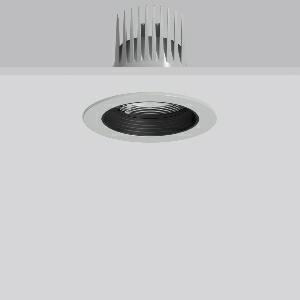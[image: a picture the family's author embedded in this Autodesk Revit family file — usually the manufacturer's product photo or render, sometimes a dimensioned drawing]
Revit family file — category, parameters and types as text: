
# Revit family: heledon_maxi_e_901768_004_cb93
name_source: partatom
category: Lighting Fixtures
units: mm (PartAtom-declared; Revit-internal decimal feet)

## family parameters
Cut with Voids When Loaded = No
Host = Face
Light Source = No
Part Type = Normal
Room Calculation Point = No
Round Connector Dimension = Use Diameter
Shared = No

## types (1)
- HELEDON maxi E (1 x LED Modul 930, 3500 lm, 3000)
    Apparent Load = 35 VA
    Approval mark = CE
    CIE Flux Codes = 96 100 100 100 100
    Color Rendering = 90
    Color Temperature = 3000
    Default Elevation = 1800 mm
    Description = Series: HELEDON maxi
Round recessed downlight. Housing: die-cast aluminium, powder-coated. Black plastic ring and recessed LED to prevent glare from the side. Optical assembly with lens made of plastic (polycarbonate) for the best homogeneous light distribution - can be changed without tools. Best colour rendering index Ra>90. Suitable for Recessed ceiling mounting. Installation without tools thanks to spring fastening system. Including separate LED converter with connecting cable 600 mm.High quality converter without flickering and stroboscopic effect. Through-wiring box (5 pole) available as accessory. The following accessories can be mounted without use of tools: interchangeable lenses, decorative glasses, honeycomb louvre, clear and frosted diffusers, white interchangeable plastic ring. 
Colour: silver
Diameter: 162 mm
Height: 3 mm
Cut-out diameter: 152 mm
Recess height: 200 mm
Luminaire: recess height: 135 mm
Lamp: LED
Socket: without socket
Colour temperature: 3000K
Colour rendering index (CRI): 92
System power: 35 W
Rated luminous flux: 3500 lm
Luminous efficiency: 100 lm/W
Control gear: Regulated power supply
Protection class: II
Type of protection: IP 20
    Height = 0 mm  [stored 0 ft]
    Lamp = 1 x LED Modul 930
    Lamp Light Flux = 3500 lm
    Lamp count = 1
    Length = 162 mm
    Lifetime = 50000 h
    Luminous efficacy = 100 lm/W
    Manufacturer = RZB
    ModVariant = No
    Model = 901768.004
    Mounting Place = Ceiling
    Mounting Type = Recessed
    Number of Poles = 1
    OnlyDefault = Yes
    Power Factor = 1
    Product Name = HELEDON maxi E
    Product group = Recessed downlights
    ProductGroupID = 402
    Protection Class = Protection class II
    Protection Degree = IP 20
    RLX_Detail_Level = 1
    RLX_Emergency_Light_Flux = 0 lm
    RLX_Emergency_Type = 0
    RLX_Emergency_Type_DB = No
    RlxData = <blob elided: 119729 chars, md5=59e6f29a>
    Socket = socket
    Standby Power = 0 W
    System Light Flux = 3500 lm
    System Power = 35 W
    Type Comments = Product without accessories
    Type Image = 901663.004.jpg
    URL = http://relux.com
    VarID = ---
    Voltage = 230 V
    Voltage Range = 220-240 V
    Weight = 0.00 kg
    Width = 0 mm  [stored 0 ft]

note: [stored X ft] marks values corroborated as IEEE doubles in the binary element streams (Revit-internal decimal feet)

## geometry (parser evidence)
native form markers: Blend x4, Sweep x9
no freeform markers — native parametric forms only
